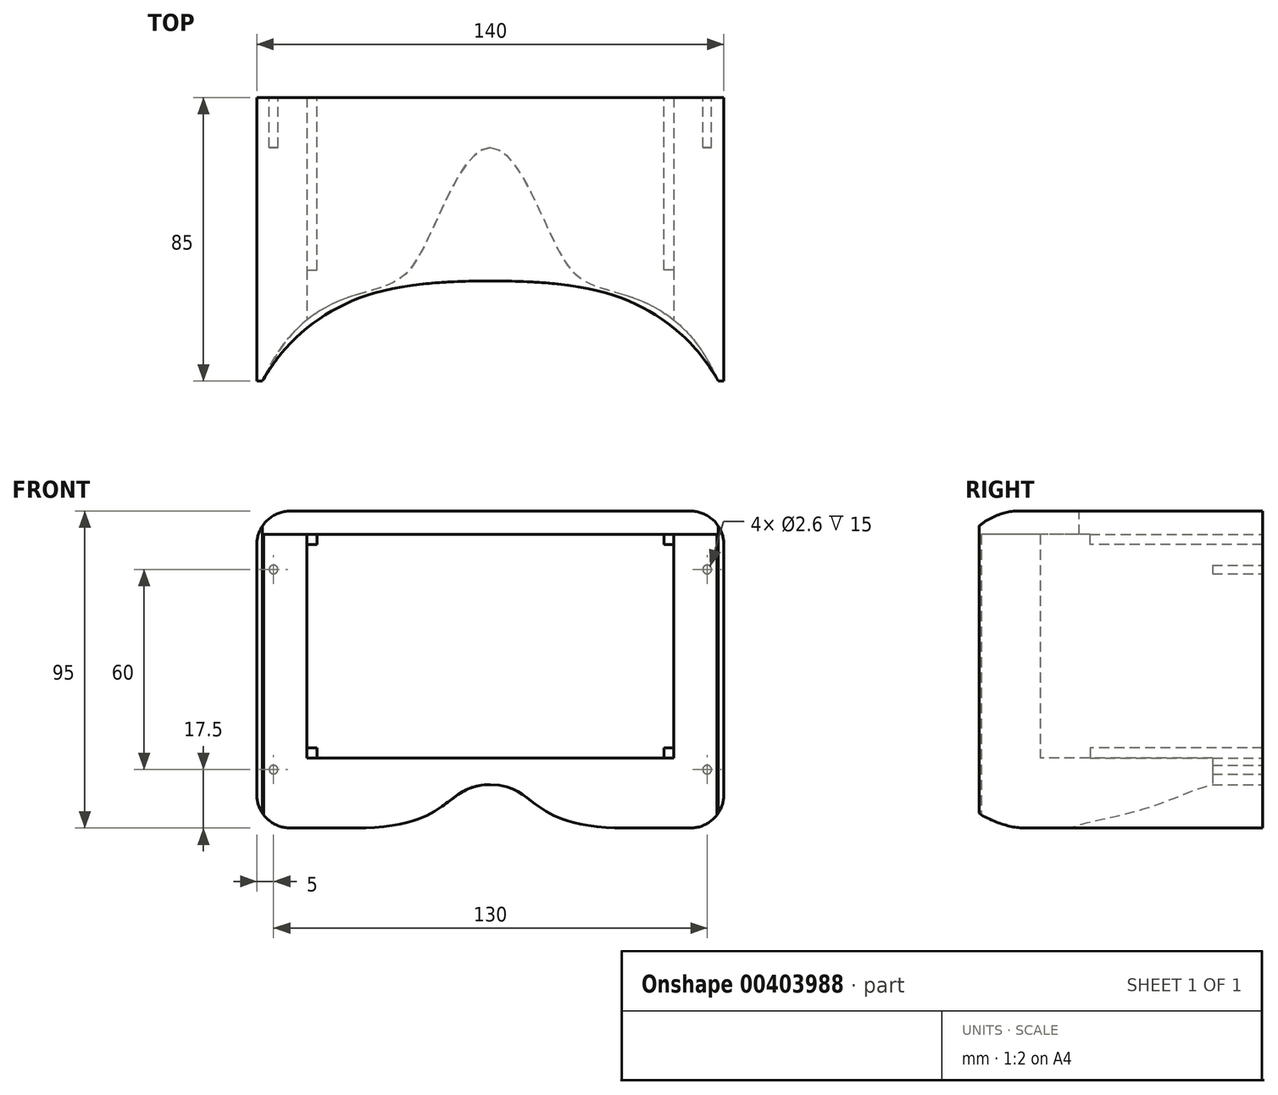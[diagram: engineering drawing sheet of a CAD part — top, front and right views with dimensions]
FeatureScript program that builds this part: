
annotation { "Feature Type Name" : "Feature", "Feature Type Description" : "" }
export const myFeature = defineFeature(function(context is Context, id is Id, definition is map)
    precondition{}
    {
        {
            var Q0;
            Q0=qCreatedBy(makeId("Top.planeOp"),FACE);
            var sketch = newSketch(context, id + "F0", { "sketchPlane" : qUnion([Q0])});
            skLineSegment(sketch, "E0.bottom", {"start": v(70, 85) * mm, "end": v(-70, 85) * mm});
            skLineSegment(sketch, "E0.top", {"start": v(70, -85) * mm, "end": v(-70, -85) * mm});
            skLineSegment(sketch, "E0.left", {"start": v(70, 85) * mm, "end": v(70, -85) * mm});
            skLineSegment(sketch, "E0.right", {"start": v(-70, 85) * mm, "end": v(-70, -85) * mm});
            skPoint(sketch, "E0.middle", {"position": v(0, 0) * mm});
            skSolve(sketch);
        }
        {
            var Q0;
            Q0=qSketchRegion(id+"F0",true);
            extrude(context, id + "F1", {"entities" : qUnion([Q0]), "depth" : 95 * mm});
        }
        {
            var Q0;
            Q0=makeQuery(id+"F1.opExtrude","SWEPT_FACE",FACE,{"disambiguationData":[OSD([sQuery(id+"F0.wireOp",EDGE,"E0.top")])]});
            var sketch = newSketch(context, id + "F2", { "sketchPlane" : qUnion([Q0])});
            skLineSegment(sketch, "E1.bottom", {"start": v(-55, 88) * mm, "end": v(55, 88) * mm});
            skLineSegment(sketch, "E1.top", {"start": v(-55, 21) * mm, "end": v(55, 21) * mm});
            skLineSegment(sketch, "E1.left", {"start": v(-55, 88) * mm, "end": v(-55, 21) * mm});
            skLineSegment(sketch, "E1.right", {"start": v(55, 88) * mm, "end": v(55, 21) * mm});
            skSolve(sketch);
        }
        {
            var Q0;
            Q0=qSketchRegion(id+"F2",true);
            extrude(context, id + "F3", {"entities" : qUnion([Q0]), "operationType" : NewBodyOperationType.REMOVE, "endBound" : BoundingType.THROUGH_ALL, "oppositeDirection" : true, "depth" : 25 * mm});
        }
        {
            var Q0;
            Q0=makeQuery(id+"F1.opExtrude","CAP_FACE",FACE,{"disambiguationData":[OSD([sQuery(id+"F0.wireOp",EDGE,"E0.bottom"),sQuery(id+"F0.wireOp",EDGE,"E0.top"),sQuery(id+"F0.wireOp",EDGE,"E0.left"),sQuery(id+"F0.wireOp",EDGE,"E0.right")])],"isStart":true});
            var sketch = newSketch(context, id + "F4", { "sketchPlane" : qUnion([Q0])});
            skLineSegment(sketch, "E2", {"start": v(0, -85) * mm, "end": v(0, 85) * mm, "construction": true});
            skLineSegment(sketch, "E3.1.0.0", {"start": v(-10, -85) * mm, "end": v(-10, 85) * mm, "construction": true});
            skLineSegment(sketch, "E3.2.0.0", {"start": v(-20, -85) * mm, "end": v(-20, 85) * mm, "construction": true});
            skLineSegment(sketch, "E3.3.0.0", {"start": v(-30, -85) * mm, "end": v(-30, 85) * mm, "construction": true});
            skLineSegment(sketch, "E3.4.0.0", {"start": v(-40, -85) * mm, "end": v(-40, 85) * mm, "construction": true});
            skLineSegment(sketch, "E3.5.0.0", {"start": v(-50, -85) * mm, "end": v(-50, 85) * mm, "construction": true});
            skLineSegment(sketch, "E3.6.0.0", {"start": v(-60, -85) * mm, "end": v(-60, 85) * mm, "construction": true});
            skLineSegment(sketch, "E3.direction1", {"start": v(0, -85) * mm, "end": v(-10, -85) * mm, "construction": true});
            skLineSegment(sketch, "E4.1.0.0", {"start": v(10, -85) * mm, "end": v(10, 85) * mm, "construction": true});
            skLineSegment(sketch, "E4.2.0.0", {"start": v(20, -85) * mm, "end": v(20, 85) * mm, "construction": true});
            skLineSegment(sketch, "E4.3.0.0", {"start": v(30, -85) * mm, "end": v(30, 85) * mm, "construction": true});
            skLineSegment(sketch, "E4.4.0.0", {"start": v(40, -85) * mm, "end": v(40, 85) * mm, "construction": true});
            skLineSegment(sketch, "E4.5.0.0", {"start": v(50, -85) * mm, "end": v(50, 85) * mm, "construction": true});
            skLineSegment(sketch, "E4.6.0.0", {"start": v(60, -85) * mm, "end": v(60, 85) * mm, "construction": true});
            skLineSegment(sketch, "E4.direction1", {"start": v(0, -85) * mm, "end": v(10, -85) * mm, "construction": true});
            skLineSegment(sketch, "E5", {"start": v(70, 15) * mm, "end": v(-70, 15) * mm, "construction": true});
            skLineSegment(sketch, "E6.0.1.0", {"start": v(70, 25) * mm, "end": v(-70, 25) * mm, "construction": true});
            skLineSegment(sketch, "E6.0.2.0", {"start": v(70, 35) * mm, "end": v(-70, 35) * mm, "construction": true});
            skLineSegment(sketch, "E6.0.3.0", {"start": v(70, 45) * mm, "end": v(-70, 45) * mm, "construction": true});
            skLineSegment(sketch, "E6.0.4.0", {"start": v(70, 55) * mm, "end": v(-70, 55) * mm, "construction": true});
            skLineSegment(sketch, "E6.0.5.0", {"start": v(70, 65) * mm, "end": v(-70, 65) * mm, "construction": true});
            skLineSegment(sketch, "E6.0.6.0", {"start": v(70, 75) * mm, "end": v(-70, 75) * mm, "construction": true});
            skLineSegment(sketch, "E6.1.0.0", {"start": v(95, 15) * mm, "end": v(-45, 15) * mm, "construction": true});
            skLineSegment(sketch, "E6.1.1.0", {"start": v(95, 25) * mm, "end": v(-45, 25) * mm, "construction": true});
            skLineSegment(sketch, "E6.1.2.0", {"start": v(95, 35) * mm, "end": v(-45, 35) * mm, "construction": true});
            skLineSegment(sketch, "E6.1.3.0", {"start": v(95, 45) * mm, "end": v(-45, 45) * mm, "construction": true});
            skLineSegment(sketch, "E6.1.4.0", {"start": v(95, 55) * mm, "end": v(-45, 55) * mm, "construction": true});
            skLineSegment(sketch, "E6.1.5.0", {"start": v(95, 65) * mm, "end": v(-45, 65) * mm, "construction": true});
            skLineSegment(sketch, "E6.1.6.0", {"start": v(95, 75) * mm, "end": v(-45, 75) * mm, "construction": true});
            skLineSegment(sketch, "E6.2.0.0", {"start": v(120, 15) * mm, "end": v(-20, 15) * mm, "construction": true});
            skLineSegment(sketch, "E6.2.1.0", {"start": v(120, 25) * mm, "end": v(-20, 25) * mm, "construction": true});
            skLineSegment(sketch, "E6.2.2.0", {"start": v(120, 35) * mm, "end": v(-20, 35) * mm, "construction": true});
            skLineSegment(sketch, "E6.2.3.0", {"start": v(120, 45) * mm, "end": v(-20, 45) * mm, "construction": true});
            skLineSegment(sketch, "E6.2.4.0", {"start": v(120, 55) * mm, "end": v(-20, 55) * mm, "construction": true});
            skLineSegment(sketch, "E6.2.5.0", {"start": v(120, 65) * mm, "end": v(-20, 65) * mm, "construction": true});
            skLineSegment(sketch, "E6.2.6.0", {"start": v(120, 75) * mm, "end": v(-20, 75) * mm, "construction": true});
            skLineSegment(sketch, "E6.direction1", {"start": v(-70, 15) * mm, "end": v(-45, 15) * mm, "construction": true});
            skLineSegment(sketch, "E6.direction2", {"start": v(-70, 15) * mm, "end": v(-70, 25) * mm, "construction": true});
            skFitSpline(sketch, "E7", {"points": [v(0, 15) * mm, v(20, 45) * mm, v(31.85, 56.6) * mm, v(68.26, 85) * mm], "startDerivative": vector(65.7, 0) * mm, "endDerivative": vector(77.5, 177.86) * mm});
            skFitSpline(sketch, "E8.MirrorCS", {"points": [v(0, 15) * mm, v(-20, 45) * mm, v(-31.85, 56.6) * mm, v(-68.26, 85) * mm], "startDerivative": vector(-65.7, 0) * mm, "endDerivative": vector(-77.5, 177.86) * mm});
            skLineSegment(sketch, "E9", {"start": v(68.26, 85) * mm, "end": v(-68.26, 85) * mm});
            skSolve(sketch);
        }
        {
            var Q0;
            Q0=makeQuery(id+"F4.imprint","IMPRINT",FACE,{"disambiguationData":[TD([[makeQuery(id+"F4.imprint","IMPRINT",EDGE,{"derivedFrom":sQuery(id+"F4.wireOp",EDGE,"E7")}),1.0]])]});
            extrude(context, id + "F5", {"entities" : qUnion([Q0]), "operationType" : NewBodyOperationType.REMOVE, "oppositeDirection" : true, "depth" : 88 * mm});
        }
        {
            var Q0;
            Q0=makeQuery(id+"F1.opExtrude","CAP_FACE",FACE,{"disambiguationData":[OSD([sQuery(id+"F0.wireOp",EDGE,"E0.bottom"),sQuery(id+"F0.wireOp",EDGE,"E0.top"),sQuery(id+"F0.wireOp",EDGE,"E0.left"),sQuery(id+"F0.wireOp",EDGE,"E0.right")])],"isStart":false});
            var sketch = newSketch(context, id + "F6", { "sketchPlane" : qUnion([Q0])});
            skLineSegment(sketch, "E10", {"start": v(-70, -55) * mm, "end": v(70, -55) * mm, "construction": true});
            skLineSegment(sketch, "E11", {"start": v(68.3, -85) * mm, "end": v(68.3, -55) * mm, "construction": true});
            skLineSegment(sketch, "E12", {"start": v(-68.36, -85) * mm, "end": v(-68.36, -55) * mm, "construction": true});
            skLineSegment(sketch, "E13", {"start": v(0, -85) * mm, "end": v(0, -55) * mm, "construction": true});
            skFitSpline(sketch, "E14", {"points": [v(0, -55) * mm, v(-47.97, -64.27) * mm, v(-68.36, -85) * mm], "startDerivative": vector(-134.93, 0) * mm, "endDerivative": vector(-37.97, -66.04) * mm});
            skFitSpline(sketch, "E15.MirrorCS", {"points": [v(0, -55) * mm, v(47.97, -64.27) * mm, v(68.36, -85) * mm], "startDerivative": vector(134.93, 0) * mm, "endDerivative": vector(37.97, -66.04) * mm});
            skLineSegment(sketch, "E16", {"start": v(-68.36, -85) * mm, "end": v(68.36, -85) * mm});
            skSolve(sketch);
        }
        {
            var Q0;
            Q0=makeQuery(id+"F6.imprint","IMPRINT",FACE,{"disambiguationData":[TD([[makeQuery(id+"F6.imprint","IMPRINT",EDGE,{"derivedFrom":sQuery(id+"F6.wireOp",EDGE,"E14")}),1.0]])]});
            extrude(context, id + "F7", {"entities" : qUnion([Q0]), "operationType" : NewBodyOperationType.REMOVE, "endBound" : BoundingType.UP_TO_NEXT, "oppositeDirection" : true, "depth" : 25 * mm});
        }
        {
            var Q0;
            Q0=makeQuery(id+"F1.opExtrude","CAP_EDGE",EDGE,{"disambiguationData":[OSD([sQuery(id+"F0.wireOp",EDGE,"E0.left")])],"isStart":false});
            var Q1;
            Q1=makeQuery(id+"F1.opExtrude","CAP_EDGE",EDGE,{"disambiguationData":[OSD([sQuery(id+"F0.wireOp",EDGE,"E0.left")])],"isStart":true});
            var Q2;
            Q2=makeQuery(id+"F1.opExtrude","CAP_EDGE",EDGE,{"disambiguationData":[OSD([sQuery(id+"F0.wireOp",EDGE,"E0.right")])],"isStart":true});
            var Q3;
            Q3=makeQuery(id+"F1.opExtrude","CAP_EDGE",EDGE,{"disambiguationData":[OSD([sQuery(id+"F0.wireOp",EDGE,"E0.right")])],"isStart":false});
            fillet(context, id + "F8", {"entities" : qUnion([Q0, Q1, Q2, Q3]), "radius" : 10 * mm, "tangentPropagation" : true, "allowEdgeOverflow" : false});
        }
        {
            var Q0;
            Q0=makeQuery(id+"F1.opExtrude","SWEPT_FACE",FACE,{"disambiguationData":[OSD([sQuery(id+"F0.wireOp",EDGE,"E0.bottom")])]});
            var sketch = newSketch(context, id + "F9", { "sketchPlane" : qUnion([Q0])});
            skLineSegment(sketch, "E17", {"start": v(0, 21) * mm, "end": v(0, 0) * mm, "construction": true});
            skLineSegment(sketch, "E18", {"start": v(-70, 13) * mm, "end": v(70, 13) * mm, "construction": true});
            skLineSegment(sketch, "E19", {"start": v(-40, 21) * mm, "end": v(-40, 0) * mm, "construction": true});
            skFitSpline(sketch, "E20", {"points": [v(0, 13) * mm, v(-40, 0) * mm], "startDerivative": vector(-42.54, 0) * mm, "endDerivative": vector(-86.95, 0) * mm});
            skFitSpline(sketch, "E21.MirrorCS", {"points": [v(0, 13) * mm, v(40, 0) * mm], "startDerivative": vector(42.54, 0) * mm, "endDerivative": vector(86.95, 0) * mm});
            skLineSegment(sketch, "E22", {"start": v(40, 0) * mm, "end": v(-40, 0) * mm});
            skSolve(sketch);
        }
        {
            var Q0;
            Q0=makeQuery(id+"F9.imprint","IMPRINT",FACE,{"disambiguationData":[TD([[makeQuery(id+"F9.imprint","IMPRINT",EDGE,{"derivedFrom":sQuery(id+"F9.wireOp",EDGE,"E20")}),1.0]])]});
            extrude(context, id + "F10", {"entities" : qUnion([Q0]), "operationType" : NewBodyOperationType.REMOVE, "endBound" : BoundingType.THROUGH_ALL, "oppositeDirection" : true, "depth" : 25 * mm});
        }
        {
            var Q0;
            Q0=makeQuery(id+"F1.opExtrude","SWEPT_FACE",FACE,{"disambiguationData":[OSD([sQuery(id+"F0.wireOp",EDGE,"E0.bottom")])]});
            var sketch = newSketch(context, id + "F11", { "sketchPlane" : qUnion([Q0])});
            skLineSegment(sketch, "E23.bottom", {"start": v(-60.5, 90) * mm, "end": v(60.5, 90) * mm});
            skLineSegment(sketch, "E23.top", {"start": v(-60.5, 14) * mm, "end": v(60.5, 14) * mm});
            skLineSegment(sketch, "E23.left", {"start": v(-60.5, 90) * mm, "end": v(-60.5, 14) * mm});
            skLineSegment(sketch, "E23.right", {"start": v(60.5, 90) * mm, "end": v(60.5, 14) * mm});
            skSolve(sketch);
        }
        {
            var Q0;
            Q0=makeQuery(id+"F11.imprint","IMPRINT",FACE,{"disambiguationData":[TD([[makeQuery(id+"F11.imprint","IMPRINT",EDGE,{"derivedFrom":sQuery(id+"F11.wireOp",EDGE,"E23.bottom")}),-1.0]])]});
            extrude(context, id + "F12", {"entities" : qUnion([Q0]), "operationType" : NewBodyOperationType.REMOVE, "oppositeDirection" : true, "depth" : 3 * mm});
        }
        {
            var Q0;
            Q0=makeQuery(id+"F3.boolean.opBoolean","COPY",FACE,{"derivedFrom":makeQuery(id+"F3.opExtrude","SWEPT_FACE",FACE,{"disambiguationData":[OSD([sQuery(id+"F2.wireOp",EDGE,"E1.top")])]})});
            var sketch = newSketch(context, id + "F13", { "sketchPlane" : qUnion([Q0])});
            skLineSegment(sketch, "E24.bottom", {"start": v(-55, -51.7) * mm, "end": v(-52, -51.7) * mm});
            skLineSegment(sketch, "E24.top", {"start": v(-55, 38.3) * mm, "end": v(-52, 38.3) * mm});
            skLineSegment(sketch, "E24.left", {"start": v(-55, -51.7) * mm, "end": v(-55, 38.3) * mm});
            skLineSegment(sketch, "E24.right", {"start": v(-52, -51.7) * mm, "end": v(-52, 38.3) * mm});
            skLineSegment(sketch, "E25.bottom", {"start": v(55, -51.7) * mm, "end": v(52, -51.7) * mm});
            skLineSegment(sketch, "E25.top", {"start": v(55, 38.3) * mm, "end": v(52, 38.3) * mm});
            skLineSegment(sketch, "E25.left", {"start": v(55, -51.7) * mm, "end": v(55, 38.3) * mm});
            skLineSegment(sketch, "E25.right", {"start": v(52, -51.7) * mm, "end": v(52, 38.3) * mm});
            skSolve(sketch);
        }
        {
            var Q0;
            Q0=qSketchRegion(id+"F13",true);
            extrude(context, id + "F14", {"entities" : qUnion([Q0]), "operationType" : NewBodyOperationType.ADD, "depth" : 3 * mm});
        }
        {
            var Q0;
            Q0=makeQuery(id+"F5.boolean.opBoolean","MERGE",FACE,{"derivedFrom":[makeQuery(id+"F3.boolean.opBoolean","COPY",FACE,{"derivedFrom":makeQuery(id+"F3.opExtrude","SWEPT_FACE",FACE,{"disambiguationData":[OSD([sQuery(id+"F2.wireOp",EDGE,"E1.bottom")])]})}),makeQuery(id+"F5.opExtrude","CAP_FACE",FACE,{"disambiguationData":[OSD([sQuery(id+"F4.wireOp",EDGE,"E7"),sQuery(id+"F4.wireOp",EDGE,"E8.MirrorCS"),sQuery(id+"F4.wireOp",EDGE,"E9")])],"isStart":false})]});
            var sketch = newSketch(context, id + "F15", { "sketchPlane" : qUnion([Q0])});
            skLineSegment(sketch, "E26.bottom", {"start": v(55, 51.7) * mm, "end": v(52, 51.7) * mm});
            skLineSegment(sketch, "E26.top", {"start": v(55, -38.3) * mm, "end": v(52, -38.3) * mm});
            skLineSegment(sketch, "E26.left", {"start": v(55, 51.7) * mm, "end": v(55, -38.3) * mm});
            skLineSegment(sketch, "E26.right", {"start": v(52, 51.7) * mm, "end": v(52, -38.3) * mm});
            skLineSegment(sketch, "E27.bottom", {"start": v(-55, 51.7) * mm, "end": v(-52, 51.7) * mm});
            skLineSegment(sketch, "E27.top", {"start": v(-55, -38.3) * mm, "end": v(-52, -38.3) * mm});
            skLineSegment(sketch, "E27.left", {"start": v(-55, 51.7) * mm, "end": v(-55, -38.3) * mm});
            skLineSegment(sketch, "E27.right", {"start": v(-52, 51.7) * mm, "end": v(-52, -38.3) * mm});
            skSolve(sketch);
        }
        {
            var Q0;
            Q0=qSketchRegion(id+"F15",true);
            extrude(context, id + "F16", {"entities" : qUnion([Q0]), "operationType" : NewBodyOperationType.ADD, "depth" : 3 * mm});
        }
        {
            var Q0;
            Q0=makeQuery(id+"F1.opExtrude","SWEPT_FACE",FACE,{"disambiguationData":[OSD([sQuery(id+"F0.wireOp",EDGE,"E0.bottom")])]});
            var sketch = newSketch(context, id + "F17", { "sketchPlane" : qUnion([Q0])});
            skLineSegment(sketch, "E28", {"start": v(-70, 47.5) * mm, "end": v(70, 47.5) * mm, "construction": true});
            skCircle(sketch, "E29", {"center": v(65, 77.5) * mm, "radius": 1.3 * mm});
            skLineSegment(sketch, "E30", {"start": v(0, 95) * mm, "end": v(0, 13) * mm, "construction": true});
            skCircle(sketch, "E31.MirrorC", {"center": v(65, 17.5) * mm, "radius": 1.3 * mm});
            skCircle(sketch, "E32.MirrorC", {"center": v(-65, 77.5) * mm, "radius": 1.3 * mm});
            skCircle(sketch, "E33.MirrorC", {"center": v(-65, 17.5) * mm, "radius": 1.3 * mm});
            skSolve(sketch);
        }
        {
            var Q0;
            Q0=qSketchRegion(id+"F17",true);
            extrude(context, id + "F18", {"entities" : qUnion([Q0]), "operationType" : NewBodyOperationType.REMOVE, "oppositeDirection" : true, "depth" : 100 * mm});
        }
        {
            var Q0;
            Q0=makeQuery(id+"F17.imprint","IMPRINT",FACE,{"disambiguationData":[TD([[makeQuery(id+"F17.imprint","IMPRINT",EDGE,{"derivedFrom":sQuery(id+"F17.wireOp",EDGE,"E29")}),-1.0]])]});
            var sketch = newSketch(context, id + "F19", { "sketchPlane" : qUnion([Q0])});
            skCircle(sketch, "E34", {"center": v(65, 77.5) * mm, "radius": 3.1 * mm});
            skCircle(sketch, "E35.MirrorC", {"center": v(65, 17.5) * mm, "radius": 3.1 * mm});
            skCircle(sketch, "E36.MirrorC", {"center": v(-65, 77.5) * mm, "radius": 3.1 * mm});
            skCircle(sketch, "E37.MirrorC", {"center": v(-65, 17.5) * mm, "radius": 3.1 * mm});
            skSolve(sketch);
        }
        {
            var Q0;
            Q0=qSketchRegion(id+"F19",true);
            extrude(context, id + "F20", {"entities" : qUnion([Q0]), "operationType" : NewBodyOperationType.REMOVE, "oppositeDirection" : true, "depth" : 75 * mm});
        }
        {
            var Q0;
            {var subQ2=sQuery(id+"F6.wireOp",EDGE,"E14");Q0=makeQuery(id+"F6.imprint","IMPRINT",FACE,{"disambiguationData":[TD([[makeQuery(id+"F6.imprint","IMPRINT",EDGE,{"derivedFrom":subQ2}),-1.0]])]});}
            var sketch = newSketch(context, id + "F21", { "sketchPlane" : qUnion([Q0])});
            skLineSegment(sketch, "E38", {"start": v(90.77, 0) * mm, "end": v(-101.48, 0) * mm, "construction": true});
            skLineSegment(sketch, "E39.bottom", {"start": v(-72.6, 0) * mm, "end": v(72.4, 0) * mm});
            skLineSegment(sketch, "E39.top", {"start": v(-72.6, 85) * mm, "end": v(72.4, 85) * mm});
            skLineSegment(sketch, "E39.left", {"start": v(-72.6, 0) * mm, "end": v(-72.6, 85) * mm});
            skLineSegment(sketch, "E39.right", {"start": v(72.4, 0) * mm, "end": v(72.4, 85) * mm});
            skSolve(sketch);
        }
        {
            var Q0;
            Q0=qSketchRegion(id+"F21",true);
            extrude(context, id + "F22", {"entities" : qUnion([Q0]), "operationType" : NewBodyOperationType.REMOVE, "endBound" : BoundingType.THROUGH_ALL, "oppositeDirection" : true, "depth" : 25 * mm});
        }
    });
